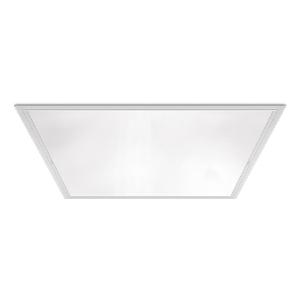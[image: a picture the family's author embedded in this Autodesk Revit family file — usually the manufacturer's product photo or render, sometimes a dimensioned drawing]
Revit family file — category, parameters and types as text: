
# Revit family: 3f_filippi_-_l_340_luce_diffusa_lgs_3f_filippi_-_23886_-_l_340_45w-940_dali_lgs_596x596
name_source: partatom
category: Lighting Fixtures
units: mm (PartAtom-declared; Revit-internal decimal feet)

## family parameters
Cut with Voids When Loaded = No
Host = Face
Light Source = No
Part Type = Normal
Room Calculation Point = No
Round Connector Dimension = Use Diameter
Shared = No

## types (1)
- 3F Filippi - L 340 Luce Diffusa LGS (1 x LED, 5066 lm, 52 W, 4000 K)
    Apparent Load = 52 VA
    Approval mark = ENEC
    CIE Flux Codes = 67 92 98 100 100
    Color Rendering = 90
    Color Temperature = 4000 K
    Control Gear = Electronic transformer
    Default Elevation = 1800 mm
    Description = ILLUMINOTECHNICAL
Luminous efficiency 100% (DLOR 100%, ULOR 0%).
Initial luminous flux of the luminaire 5066 lm.
Direct symmetric distribution.
Installation Interdistance Transv.D = 1.19 x hu - Long.D = 1.17 x hu.
Average luminance <3000 cd/m² for radial angles >65°.
Tabular UGR (CIE 117 - 4H-8H; S=0.25H; 70/50/20): RUG 17.4 - 17.5.
Beam angle: 87° - 86°.
Luminous efficacy 97 lm/W.
Lifetime (L93/B10): 30000 h. (tq+25°C)
Lifetime (L90/B10): 50000 h. (tq+25°C)
Lifetime (L85/B10): 80000 h. (tq+25°C)
Lifetime (L80/B10): 100000 h. (tq+25°C)
Sudden decreased luminous flux after 50000 hours: 0% (C0).
Photobiological safety in compliance with IEC/TR 62778: RG0 risk exempt, (IEC 62471).
In compliance with IEC/EN 62722-2-1 - IEC/EN 62717 standards.

SOURCE
Squared LED module 45W/940.
Energy efficiency class (UE 2019/2020 - UE 2019/2015): D.
CIE 13.3 Colour rendering index: CRI >90 (R9 >50%).
IES TM-30 Fidelity Index: Rf = 92 Rg = 101.
CCT nominal colour temperature 4000 K.
Colour initial tolerance (MacAdam): SDCM 3.

MECHANICAL
Housing in hot-galvanised steel, painted in white polyester.
Perimetral frame in white polycarbonate.
LGS micro-prismatic flat diffuser in transparent methacrylate (PMMA), multi-lenticular exterior, anti-glare.
Anti-glare opal polycarbonate filter for brightness uniformity.
Luminaire with limited surface temperature. - D - (EN 60598-2-24)
Dimensions: 596x596 mm, height 80 mm. Weight 4.4 kg.
IP40 protection degree.
Mechanical strength to impacts IK06 (1 joule).
Glow-wire test resistance 650°C.

ELECTRICAL
Wiring on a separate unit.
Halogen Free DALI-2 DATI (Parts 251, 252, 253), PUSH-DIM, electronic wiring 230V-50/60Hz, power factor 0.95 at full load, THD <25%, constant output current, SELV, class II, 1 driver, 1 DALI addresse.
Power of the luminaire 52 W.
CE - IEC 60598-1 - EN 60598-1.
SAFE FLICKER: PstLM=<1 and SVM=<0.4 (IEC TR 61547-1 and IEC TR 63158), to ensure a more comfortable and safe light.
Luminaire compliant with EN 60598-2-22 for power supply from a centralised emergency system CPSS (Central Power Supply System), not incorporated in the luminaire - high risk areas excluded. The default power and flux are 100% in AC and 15% in DC.
Ambient temperature from 0°C to +40°C.
Temperature class T6 max 85°C.
Relative humidity UR: <85%.

INSTALLATION
Lay-on or pull-up recessed fitting using frame accessory.
All accessories dedicated to this product are available on the Catalog and on our website www.3F-Filippi.com.

APPLICATIONS
Suitable product for food production plants (HACCP), IFS (Food Version 6), BRC (GSFS Food Version 7).
Environments: with VDTs, meeting rooms, offices.
Environments: architectural, commercial, staterooms, banks.
Environments where demanding visual tasks are performed and soft diffuse light is required for optimal visual comfort and total shielding of the light source.

LIGHT MANAGEMENT
Recommended minimum setting: 10%.
The luminaire, equipped with (DALI-2 DATI) driver, can be controlled manually with 3F Easy Dim technology or automatically/manually with wired or wireless DALI/D2D control systems.
The D2D driver guarantees interoperability with other devices with the same certification by making the following information available:
Device Data (Part 251), Energy Report (Part 252), Diagnosis & Maintenance (Part 253).
In electrical systems without a regulation system (manual or automatic) and DALI bus, a suitable jumper must be made on the DA-DA terminals of the appliance.

WARNING
Luminaire designed for disposal/recycling at end-of-life.
Replaceable (LED only) light source by a professional. Replaceable control gear by a professional.
    Height = 0 mm  [stored 0 ft]
    Lamp = 1 x LED
    Lamp Light Flux = 5066 lm
    Lamp Power = 52 W
    Lamp count = 1
    Length = 596 mm
    Lifetime = 50000 h
    Luminous efficacy = 97 lm/W
    Manufacturer = 3F Filippi
    ModVariant = No
    Model = 3F Filippi - 23886 - L 340 45W-940 DALI LGS 596x596
    Mounting Place = Ceiling
    Mounting Type = Recessed
    Number of Poles = 1
    OnlyDefault = Yes
    Power Factor = 1
    Product Name = 3F Filippi - L 340 Luce Diffusa LGS
    Product group = recessed luminaire
    ProductGroupID = 4
    Protection Class = Protection class II
    Protection Degree = IP 40
    RLX_Detail_Level = 1
    RLX_Emergency_Light_Flux = 0 lm
    RLX_Emergency_Type = 0
    RLX_Emergency_Type_DB = No
    RlxData = <blob elided: 155881 chars, md5=394dc471>
    Socket = socket
    Standby Power = 0 W
    System Light Flux = 5066 lm
    System Power = 52 W
    Type Comments = Product without accessories
    Type Image = 3ffilippi_l_340_luce_diffusa_lgs.jpg
    URL = http://relux.com
    VarID = ---
    Voltage = 0 V
    Weight = 0.00 kg
    Width = 596 mm

note: [stored X ft] marks values corroborated as IEEE doubles in the binary element streams (Revit-internal decimal feet)

## geometry (parser evidence)
native form markers: Blend x4, Sweep x12
no freeform markers — native parametric forms only
